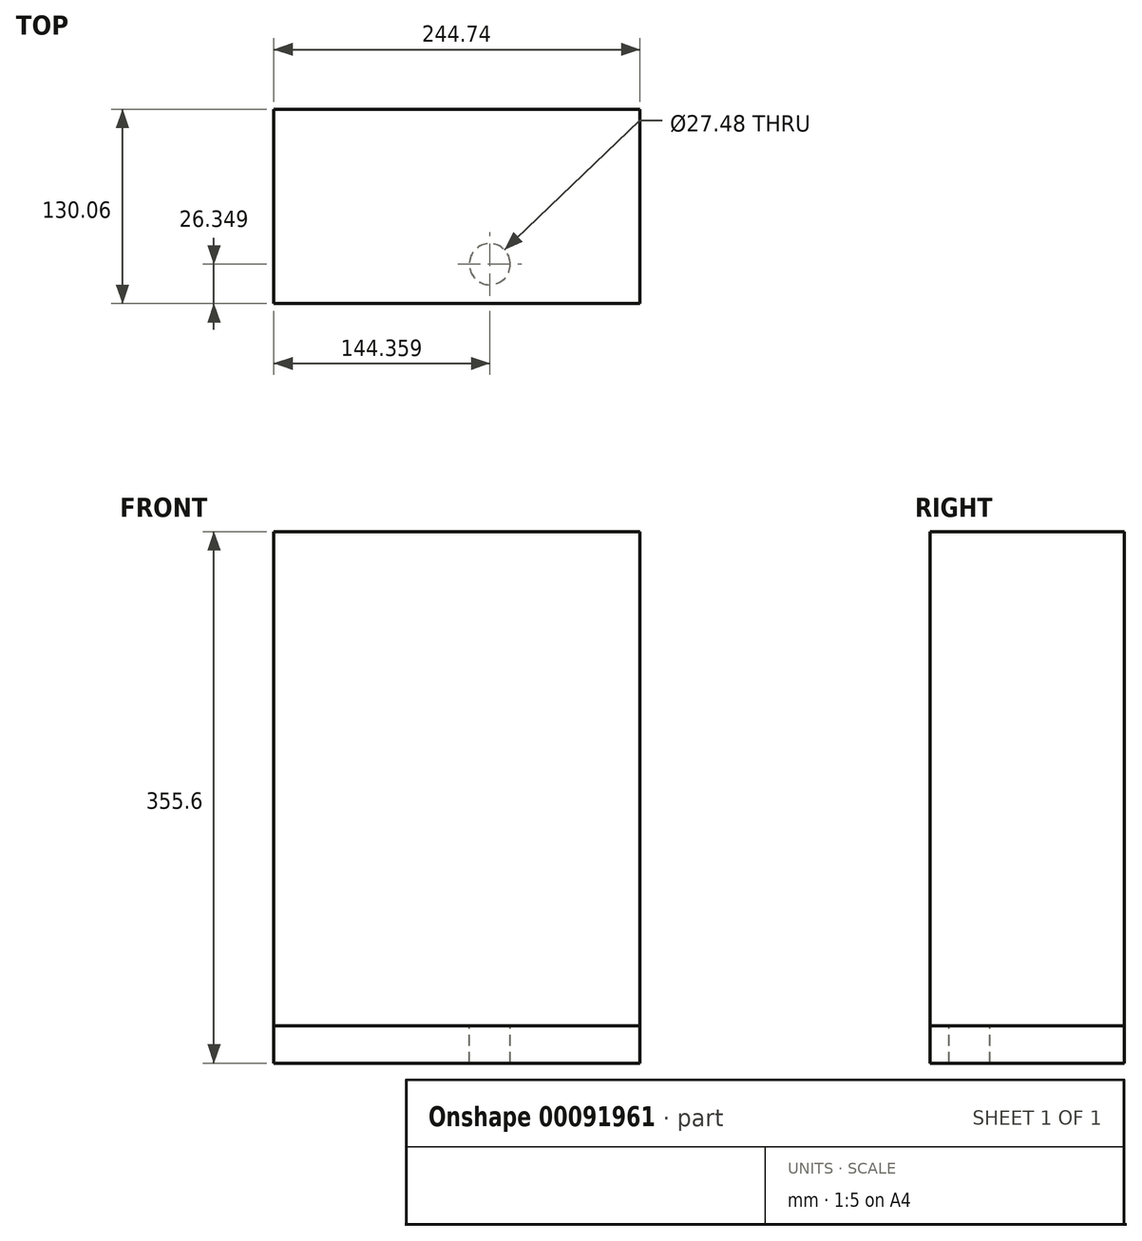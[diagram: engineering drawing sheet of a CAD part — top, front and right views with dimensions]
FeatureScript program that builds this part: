
annotation { "Feature Type Name" : "Feature", "Feature Type Description" : "" }
export const myFeature = defineFeature(function(context is Context, id is Id, definition is map)
    precondition{}
    {
        {
            var Q0;
            Q0=qCreatedBy(makeId("Top.planeOp"),FACE);
            var sketch = newSketch(context, id + "F0", { "sketchPlane" : qUnion([Q0])});
            skLineSegment(sketch, "E0.bottom", {"start": v(-122.37, -65.03) * mm, "end": v(122.37, -65.03) * mm});
            skLineSegment(sketch, "E0.top", {"start": v(-122.37, 65.03) * mm, "end": v(122.37, 65.03) * mm});
            skLineSegment(sketch, "E0.left", {"start": v(-122.37, -65.03) * mm, "end": v(-122.37, 65.03) * mm});
            skLineSegment(sketch, "E0.right", {"start": v(122.37, -65.03) * mm, "end": v(122.37, 65.03) * mm});
            skPoint(sketch, "E0.middle", {"position": v(0, 0) * mm});
            skSolve(sketch);
        }
        {
            var Q0;
            Q0=makeQuery(id+"F0.imprint","IMPRINT",FACE,{"disambiguationData":[TD([[makeQuery(id+"F0.imprint","IMPRINT",EDGE,{"derivedFrom":sQuery(id+"F0.wireOp",EDGE,"E0.bottom")}),1.0]])]});
            extrude(context, id + "F1", {"entities" : qUnion([Q0]), "depth" : 25 * mm});
        }
        {
            var Q0;
            Q0=makeQuery(id+"F1.opExtrude","CAP_FACE",FACE,{"disambiguationData":[OSD([sQuery(id+"F0.wireOp",EDGE,"E0.bottom"),sQuery(id+"F0.wireOp",EDGE,"E0.top"),sQuery(id+"F0.wireOp",EDGE,"E0.left"),sQuery(id+"F0.wireOp",EDGE,"E0.right")])],"isStart":false});
            var sketch = newSketch(context, id + "F2", { "sketchPlane" : qUnion([Q0])});
            skCircle(sketch, "E1", {"center": v(22.2, -37.87) * mm, "radius": 19.39 * mm});
            skSolve(sketch);
        }
        {
            var Q0;
            Q0 = qSketchRegion(id + "F2", true);
            var Q1;
            Q1=makeQuery(id+"F2.imprint","IMPRINT",FACE,{"disambiguationData":[TD([[makeQuery(id+"F2.imprint","IMPRINT",EDGE,{"derivedFrom":sQuery(id+"F2.wireOp",EDGE,"E1")}),1.0]])]});
            extrude(context, id + "F3", {"entities" : qUnion([Q0, Q1]), "operationType" : NewBodyOperationType.ADD, "oppositeDirection" : true, "depth" : 25 * mm});
        }
        {
            var Q0;
            Q0=makeQuery(id+"F1.opExtrude","CAP_FACE",FACE,{"disambiguationData":[OSD([sQuery(id+"F0.wireOp",EDGE,"E0.bottom"),sQuery(id+"F0.wireOp",EDGE,"E0.top"),sQuery(id+"F0.wireOp",EDGE,"E0.left"),sQuery(id+"F0.wireOp",EDGE,"E0.right")])],"isStart":false});
            var sketch = newSketch(context, id + "F4", { "sketchPlane" : qUnion([Q0])});
            skCircle(sketch, "E2", {"center": v(21.99, -38.68) * mm, "radius": 13.74 * mm});
            skSolve(sketch);
        }
        {
            var Q0;
            Q0=makeQuery(id+"F4.imprint","IMPRINT",FACE,{"disambiguationData":[TD([[makeQuery(id+"F4.imprint","IMPRINT",EDGE,{"derivedFrom":sQuery(id+"F4.wireOp",EDGE,"E2")}),1.0]])]});
            extrude(context, id + "F5", {"entities" : qUnion([Q0]), "operationType" : NewBodyOperationType.REMOVE, "oppositeDirection" : true, "depth" : 25.25 * mm});
        }
        {
            var Q0;
            Q0=makeQuery(id+"F0.imprint","IMPRINT",FACE,{"disambiguationData":[TD([[makeQuery(id+"F0.imprint","IMPRINT",EDGE,{"derivedFrom":sQuery(id+"F0.wireOp",EDGE,"E0.bottom")}),1.0]])]});
            extrude(context, id + "F6", {"entities" : qUnion([Q0]), "depth" : 355.6 * mm});
        }
    });
